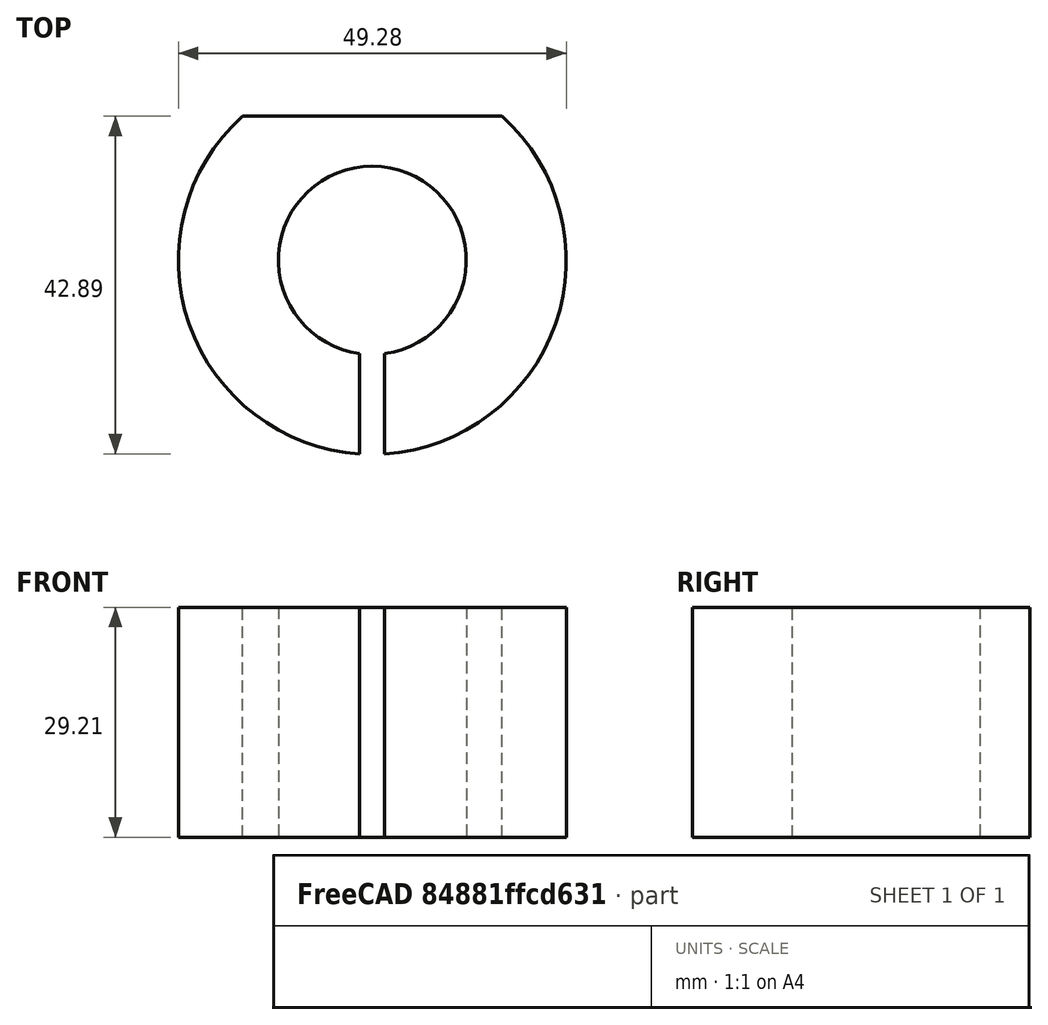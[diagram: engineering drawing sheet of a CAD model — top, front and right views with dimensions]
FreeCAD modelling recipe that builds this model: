
FCSTD DOCUMENT  (FreeCAD 0.15R4671 (Git))
Label: motor_mount
License: All rights reserved
LicenseURL: http://en.wikipedia.org/wiki/All_rights_reserved
objects: Sketcher::SketchObject×1, PartDesign::Pad×1
note: 3 computed .brp shape members not serialized (recipe doc carries the construction recipe); baked Part::Feature solids carry a one-line shape summary decoded from their .brp

FEATURE [Sketcher::SketchObject] Sketch
  sketch-geometry (6):
    g0: ArcOfCircle CenterX=0 CenterY=0 CenterZ=0 NormalX=0 NormalY=0 NormalZ=1 Radius=11.9405 StartAngle=4.84573 EndAngle=10.8622
    g1: ArcOfCircle CenterX=0 CenterY=0 CenterZ=0 NormalX=0 NormalY=0 NormalZ=1 Radius=24.6405 StartAngle=4.77686 EndAngle=7.12005
    g2: LineSegment StartX=-1.5875 StartY=-11.8345 StartZ=0 EndX=-1.5875 EndY=-24.5893 EndZ=0
    g3: LineSegment StartX=1.5875 StartY=-11.8345 StartZ=0 EndX=1.5875 EndY=-24.5893 EndZ=0
    g4: ArcOfCircle CenterX=0 CenterY=0 CenterZ=0 NormalX=0 NormalY=0 NormalZ=1 Radius=24.6405 StartAngle=2.30473 EndAngle=4.64792
    g5: LineSegment StartX=-16.5041 StartY=18.2968 StartZ=0 EndX=16.5041 EndY=18.2968 EndZ=0
  constraints (22):
    c: Radius(g0) = 11.9405
    c: Coincident(g1,g-1)
    c: Radius(g1) = 24.6405
    c: Coincident(g0,g-1)
    c: Vertical(g2)
    c: Vertical(g3)
    c: Equal(g2,g3)
    c: DistanceX(g3,g2) = -3.175
    c: DistanceX(g-1,g3) = 1.5875
    c: PointOnObject(g0,g3)
    c: PointOnObject(g0,g2)
    c: PointOnObject(g1,g3)
    c: PointOnObject(g4,g2)
    c: Coincident(g2,g0)
    c: Coincident(g4,g2)
    c: Coincident(g3,g0)
    c: Equal(g1,g4)
    c: Coincident(g1,g4)
    c: Horizontal(g5)
    c: Coincident(g5,g4)
    c: Coincident(g1,g5)
    c: DistanceY(g-1,g1) = 18.2968
FEATURE [PartDesign::Pad] Pad
  Length = 29.21
  Length2 = 100
  Sketch = -> Sketch
  Type = 0
